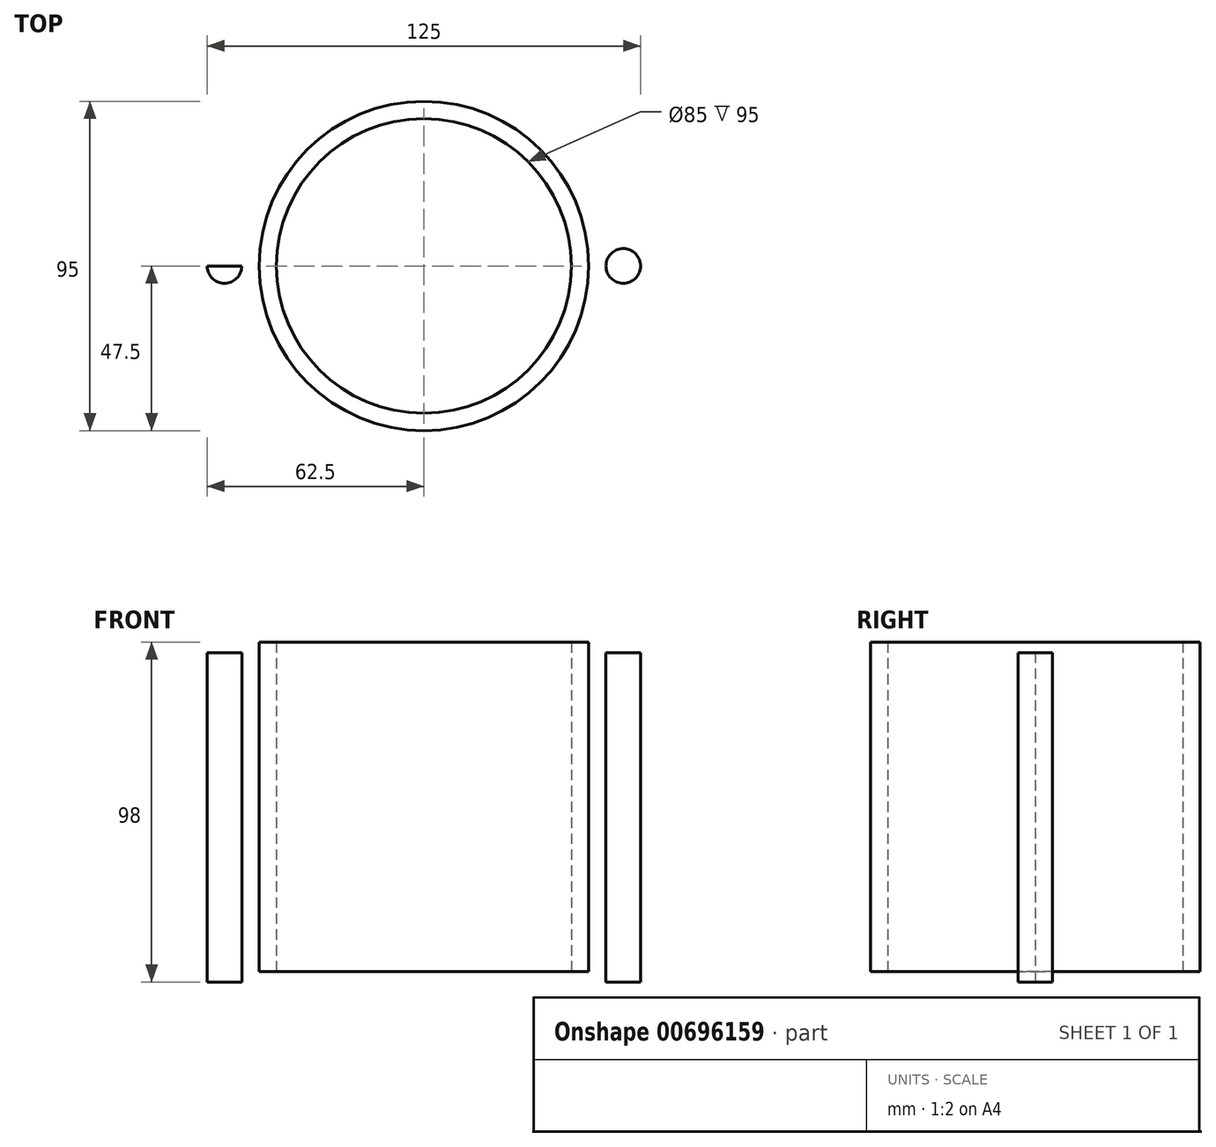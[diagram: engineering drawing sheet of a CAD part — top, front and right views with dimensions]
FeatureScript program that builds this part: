
annotation { "Feature Type Name" : "Feature", "Feature Type Description" : "" }
export const myFeature = defineFeature(function(context is Context, id is Id, definition is map)
    precondition{}
    {
        {
            var Q0;
            Q0=qCreatedBy(makeId("Top.planeOp"),FACE);
            var sketch = newSketch(context, id + "F0", { "sketchPlane" : qUnion([Q0])});
            skLineSegment(sketch, "E0.bottom", {"start": v(-70, 70) * mm, "end": v(70, 70) * mm});
            skLineSegment(sketch, "E0.top", {"start": v(-70, -70) * mm, "end": v(70, -70) * mm});
            skLineSegment(sketch, "E0.left", {"start": v(-70, 70) * mm, "end": v(-70, -70) * mm});
            skLineSegment(sketch, "E0.right", {"start": v(70, 70) * mm, "end": v(70, -70) * mm});
            skCircle(sketch, "E1", {"center": v(0, 0) * mm, "radius": 42.5 * mm});
            skSolve(sketch);
        }
        {
            var Q0;
            Q0=qSketchRegion(id+"F0",true);
            extrude(context, id + "F1", {"entities" : qUnion([Q0]), "depth" : 95 * mm});
        }
        {
            var Q0;
            Q0=makeQuery(id+"F1.opExtrude","CAP_FACE",FACE,{"disambiguationData":[OSD([sQuery(id+"F0.wireOp",EDGE,"E0.bottom"),sQuery(id+"F0.wireOp",EDGE,"E0.top"),sQuery(id+"F0.wireOp",EDGE,"E0.left"),sQuery(id+"F0.wireOp",EDGE,"E0.right"),sQuery(id+"F0.wireOp",EDGE,"E1")])],"isStart":false});
            var sketch = newSketch(context, id + "F2", { "sketchPlane" : qUnion([Q0])});
            skCircle(sketch, "E2", {"center": v(0, 0) * mm, "radius": 47.5 * mm});
            skCircle(sketch, "E3", {"center": v(0, 0) * mm, "radius": 42.5 * mm});
            skSolve(sketch);
        }
        {
            var Q0;
            Q0=qSketchRegion(id+"F2",true);
            extrude(context, id + "F3", {"entities" : qUnion([Q0]), "operationType" : NewBodyOperationType.ADD, "depth" : 3 * mm, "offsetDistance" : 25 * mm});
        }
        {
            var Q0;
            Q0=makeQuery(id+"F1.opExtrude","CAP_FACE",FACE,{"disambiguationData":[OSD([sQuery(id+"F0.wireOp",EDGE,"E0.bottom"),sQuery(id+"F0.wireOp",EDGE,"E0.top"),sQuery(id+"F0.wireOp",EDGE,"E0.left"),sQuery(id+"F0.wireOp",EDGE,"E0.right"),sQuery(id+"F0.wireOp",EDGE,"E1")])],"isStart":true});
            var sketch = newSketch(context, id + "F4", { "sketchPlane" : qUnion([Q0])});
            skCircle(sketch, "E4", {"center": v(0, 0) * mm, "radius": 47.5 * mm});
            skCircle(sketch, "E5", {"center": v(0, 0) * mm, "radius": 42.5 * mm});
            skSolve(sketch);
        }
        {
            var Q0;
            Q0=qSketchRegion(id+"F4",true);
            extrude(context, id + "F5", {"entities" : qUnion([Q0]), "operationType" : NewBodyOperationType.REMOVE, "oppositeDirection" : true, "depth" : 3 * mm, "offsetDistance" : 25 * mm});
        }
        {
            var Q0;
            Q0=makeQuery(id+"F1.opExtrude","CAP_FACE",FACE,{"disambiguationData":[OSD([sQuery(id+"F0.wireOp",EDGE,"E0.bottom"),sQuery(id+"F0.wireOp",EDGE,"E0.top"),sQuery(id+"F0.wireOp",EDGE,"E0.left"),sQuery(id+"F0.wireOp",EDGE,"E0.right"),sQuery(id+"F0.wireOp",EDGE,"E1")])],"isStart":true});
            var sketch = newSketch(context, id + "F6", { "sketchPlane" : qUnion([Q0])});
            skCircle(sketch, "E6", {"center": v(0, 0) * mm, "radius": 65 * mm});
            skLineSegment(sketch, "E7", {"start": v(0, 0) * mm, "end": v(-70, -70) * mm});
            skLineSegment(sketch, "E8.anchor1", {"start": v(0, 0) * mm, "end": v(-45.96, -45.96) * mm, "construction": true});
            skLineSegment(sketch, "E8.anchor2", {"start": v(0, 0) * mm, "end": v(-45.96, 45.96) * mm, "construction": true});
            skPoint(sketch, "E9", {"position": v(-45.96, -45.96) * mm});
            skPoint(sketch, "E10", {"position": v(-45.96, 45.96) * mm});
            skPoint(sketch, "E11", {"position": v(45.96, -45.96) * mm});
            skPoint(sketch, "E12.2.0", {"position": v(45.96, 45.96) * mm});
            skSolve(sketch);
        }
        {
            var Q0;
            Q0=makeQuery(id+"F1.opExtrude","CAP_FACE",FACE,{"disambiguationData":[OSD([sQuery(id+"F0.wireOp",EDGE,"E0.bottom"),sQuery(id+"F0.wireOp",EDGE,"E0.top"),sQuery(id+"F0.wireOp",EDGE,"E0.left"),sQuery(id+"F0.wireOp",EDGE,"E0.right"),sQuery(id+"F0.wireOp",EDGE,"E1")])],"isStart":true});
            var sketch = newSketch(context, id + "F7", { "sketchPlane" : qUnion([Q0])});
            skCircle(sketch, "E13", {"center": v(0, 0) * mm, "radius": 57.5 * mm});
            skLineSegment(sketch, "E14", {"start": v(0, 0) * mm, "end": v(-64.85, 0) * mm});
            skCircle(sketch, "E15", {"center": v(-57.5, 0) * mm, "radius": 5 * mm});
            skCircle(sketch, "E16.1.0", {"center": v(0, -57.5) * mm, "radius": 5 * mm});
            skCircle(sketch, "E16.2.0", {"center": v(57.5, 0) * mm, "radius": 5 * mm});
            skCircle(sketch, "E16.3.0", {"center": v(0, 57.5) * mm, "radius": 5 * mm});
            skLineSegment(sketch, "E16.anchor1", {"start": v(0, 0) * mm, "end": v(-57.5, 0) * mm, "construction": true});
            skLineSegment(sketch, "E16.anchor2", {"start": v(0, 0) * mm, "end": v(0, 57.5) * mm, "construction": true});
            skSolve(sketch);
        }
        {
            var Q0;
            {var subQ0=sQuery(id+"F7.wireOp",EDGE,"E14");var subQ1=sQuery(id+"F7.wireOp",EDGE,"E13");var subQ2=makeQuery(id+"F7.imprint","INTERSECT",VERTEX,{"derivedFrom":[subQ1,subQ0]});Q0=makeQuery(id+"F7.imprint","IMPRINT",FACE,{"disambiguationData":[TD([[makeQuery(id+"F7.imprint","IMPRINT",EDGE,{"disambiguationData":[TD([[subQ2,-1.0]])],"derivedFrom":subQ1}),-1.0]])]});}
            var Q1;
            {var subQ0=sQuery(id+"F7.wireOp",EDGE,"E14");var subQ1=sQuery(id+"F7.wireOp",EDGE,"E13");var subQ2=makeQuery(id+"F7.imprint","INTERSECT",VERTEX,{"derivedFrom":[subQ1,subQ0]});Q1=makeQuery(id+"F7.imprint","IMPRINT",FACE,{"disambiguationData":[TD([[makeQuery(id+"F7.imprint","IMPRINT",EDGE,{"disambiguationData":[TD([[subQ2,-1.0]])],"derivedFrom":subQ1}),1.0]])]});}
            var Q2;
            {var subQ0=sQuery(id+"F7.wireOp",EDGE,"E15");var subQ1=sQuery(id+"F7.wireOp",EDGE,"E13");var subQ2=makeQuery(id+"F7.imprint","INTERSECT",VERTEX,{"disambiguationData":[OD(0.0)],"derivedFrom":[subQ1,subQ0]});Q2=makeQuery(id+"F7.imprint","IMPRINT",FACE,{"disambiguationData":[TD([[makeQuery(id+"F7.imprint","IMPRINT",EDGE,{"disambiguationData":[TD([[subQ2,-1.0]])],"derivedFrom":subQ1}),1.0]])]});}
            var Q3;
            {var subQ0=sQuery(id+"F7.wireOp",EDGE,"E15");var subQ1=sQuery(id+"F7.wireOp",EDGE,"E13");var subQ2=makeQuery(id+"F7.imprint","INTERSECT",VERTEX,{"disambiguationData":[OD(0.0)],"derivedFrom":[subQ1,subQ0]});Q3=makeQuery(id+"F7.imprint","IMPRINT",FACE,{"disambiguationData":[TD([[makeQuery(id+"F7.imprint","IMPRINT",EDGE,{"disambiguationData":[TD([[subQ2,-1.0]])],"derivedFrom":subQ1}),-1.0]])]});}
            var Q4;
            {var subQ0=sQuery(id+"F7.wireOp",EDGE,"E16.1.0");var subQ1=sQuery(id+"F7.wireOp",EDGE,"E13");var subQ2=makeQuery(id+"F7.imprint","INTERSECT",VERTEX,{"disambiguationData":[OD(0.0)],"derivedFrom":[subQ1,subQ0]});Q4=makeQuery(id+"F7.imprint","IMPRINT",FACE,{"disambiguationData":[TD([[makeQuery(id+"F7.imprint","IMPRINT",EDGE,{"disambiguationData":[TD([[subQ2,-1.0]])],"derivedFrom":subQ1}),1.0]])]});}
            var Q5;
            {var subQ0=sQuery(id+"F7.wireOp",EDGE,"E16.1.0");var subQ1=sQuery(id+"F7.wireOp",EDGE,"E13");var subQ2=makeQuery(id+"F7.imprint","INTERSECT",VERTEX,{"disambiguationData":[OD(0.0)],"derivedFrom":[subQ1,subQ0]});Q5=makeQuery(id+"F7.imprint","IMPRINT",FACE,{"disambiguationData":[TD([[makeQuery(id+"F7.imprint","IMPRINT",EDGE,{"disambiguationData":[TD([[subQ2,-1.0]])],"derivedFrom":subQ1}),-1.0]])]});}
            var Q6;
            {var subQ0=sQuery(id+"F7.wireOp",EDGE,"E16.2.0");var subQ1=sQuery(id+"F7.wireOp",EDGE,"E13");var subQ2=makeQuery(id+"F7.imprint","INTERSECT",VERTEX,{"disambiguationData":[OD(0.0)],"derivedFrom":[subQ1,subQ0]});Q6=makeQuery(id+"F7.imprint","IMPRINT",FACE,{"disambiguationData":[TD([[makeQuery(id+"F7.imprint","IMPRINT",EDGE,{"disambiguationData":[TD([[subQ2,1.0]])],"derivedFrom":subQ1}),-1.0]])]});}
            var Q7;
            {var subQ0=sQuery(id+"F7.wireOp",EDGE,"E16.2.0");var subQ1=sQuery(id+"F7.wireOp",EDGE,"E13");var subQ2=makeQuery(id+"F7.imprint","INTERSECT",VERTEX,{"disambiguationData":[OD(0.0)],"derivedFrom":[subQ1,subQ0]});Q7=makeQuery(id+"F7.imprint","IMPRINT",FACE,{"disambiguationData":[TD([[makeQuery(id+"F7.imprint","IMPRINT",EDGE,{"disambiguationData":[TD([[subQ2,1.0]])],"derivedFrom":subQ1}),1.0]])]});}
            var Q8;
            {var subQ0=sQuery(id+"F7.wireOp",EDGE,"E16.3.0");var subQ1=sQuery(id+"F7.wireOp",EDGE,"E13");var subQ2=makeQuery(id+"F7.imprint","INTERSECT",VERTEX,{"disambiguationData":[OD(0.0)],"derivedFrom":[subQ1,subQ0]});Q8=makeQuery(id+"F7.imprint","IMPRINT",FACE,{"disambiguationData":[TD([[makeQuery(id+"F7.imprint","IMPRINT",EDGE,{"disambiguationData":[TD([[subQ2,-1.0]])],"derivedFrom":subQ1}),1.0]])]});}
            var Q9;
            {var subQ0=sQuery(id+"F7.wireOp",EDGE,"E16.3.0");var subQ1=sQuery(id+"F7.wireOp",EDGE,"E13");var subQ2=makeQuery(id+"F7.imprint","INTERSECT",VERTEX,{"disambiguationData":[OD(0.0)],"derivedFrom":[subQ1,subQ0]});Q9=makeQuery(id+"F7.imprint","IMPRINT",FACE,{"disambiguationData":[TD([[makeQuery(id+"F7.imprint","IMPRINT",EDGE,{"disambiguationData":[TD([[subQ2,-1.0]])],"derivedFrom":subQ1}),-1.0]])]});}
            var Q10;
            Q10=sQuery(id+"F7.wireOp",EDGE,"E15");
            var Q11;
            Q11=sQuery(id+"F7.wireOp",EDGE,"E16.1.0");
            var Q12;
            Q12=sQuery(id+"F7.wireOp",EDGE,"E16.2.0");
            var Q13;
            Q13=sQuery(id+"F7.wireOp",EDGE,"E16.3.0");
            extrude(context, id + "F8", {"entities" : qUnion([Q0, Q1, Q2, Q3, Q4, Q5, Q6, Q7, Q8, Q9]), "operationType" : NewBodyOperationType.REMOVE, "surfaceEntities" : qUnion([Q10, Q11, Q12, Q13]), "endBound" : BoundingType.THROUGH_ALL, "oppositeDirection" : true, "depth" : 25 * mm, "offsetDistance" : 25 * mm});
        }
        {
            var Q0;
            Q0=sQuery(id+"F6.wireOp",VERTEX,"E9");
            var Q1;
            Q1=sQuery(id+"F6.wireOp",VERTEX,"E10");
            var Q2;
            Q2=sQuery(id+"F6.wireOp",VERTEX,"E11");
            var Q3;
            Q3=sQuery(id+"F6.wireOp",VERTEX,"E12.2.0");
            var Q4;
            Q4=makeQuery(id+"F1.opExtrude","SWEPT_BODY",BODY,{"disambiguationData":[OSD([sQuery(id+"F0.wireOp",EDGE,"E0.bottom"),sQuery(id+"F0.wireOp",EDGE,"E0.top"),sQuery(id+"F0.wireOp",EDGE,"E0.left"),sQuery(id+"F0.wireOp",EDGE,"E0.right"),sQuery(id+"F0.wireOp",EDGE,"E1")])]});
            hole(context, id + "F9", {"style" : HoleStyle.C_BORE, "endStyle" : HoleEndStyle.THROUGH, "holeDiameter" : 6 * mm, "cBoreDiameter" : 20 * mm, "cBoreDepth" : 30 * mm, "majorDiameter" : 5 * mm, "isTappedThrough" : true, "tappedDepth" : 12 * mm, "tapClearance" : 3, "startFromSketch" : true, "locations" : qUnion([Q0, Q1, Q2, Q3]), "scope" : qUnion([Q4])});
        }
    });
